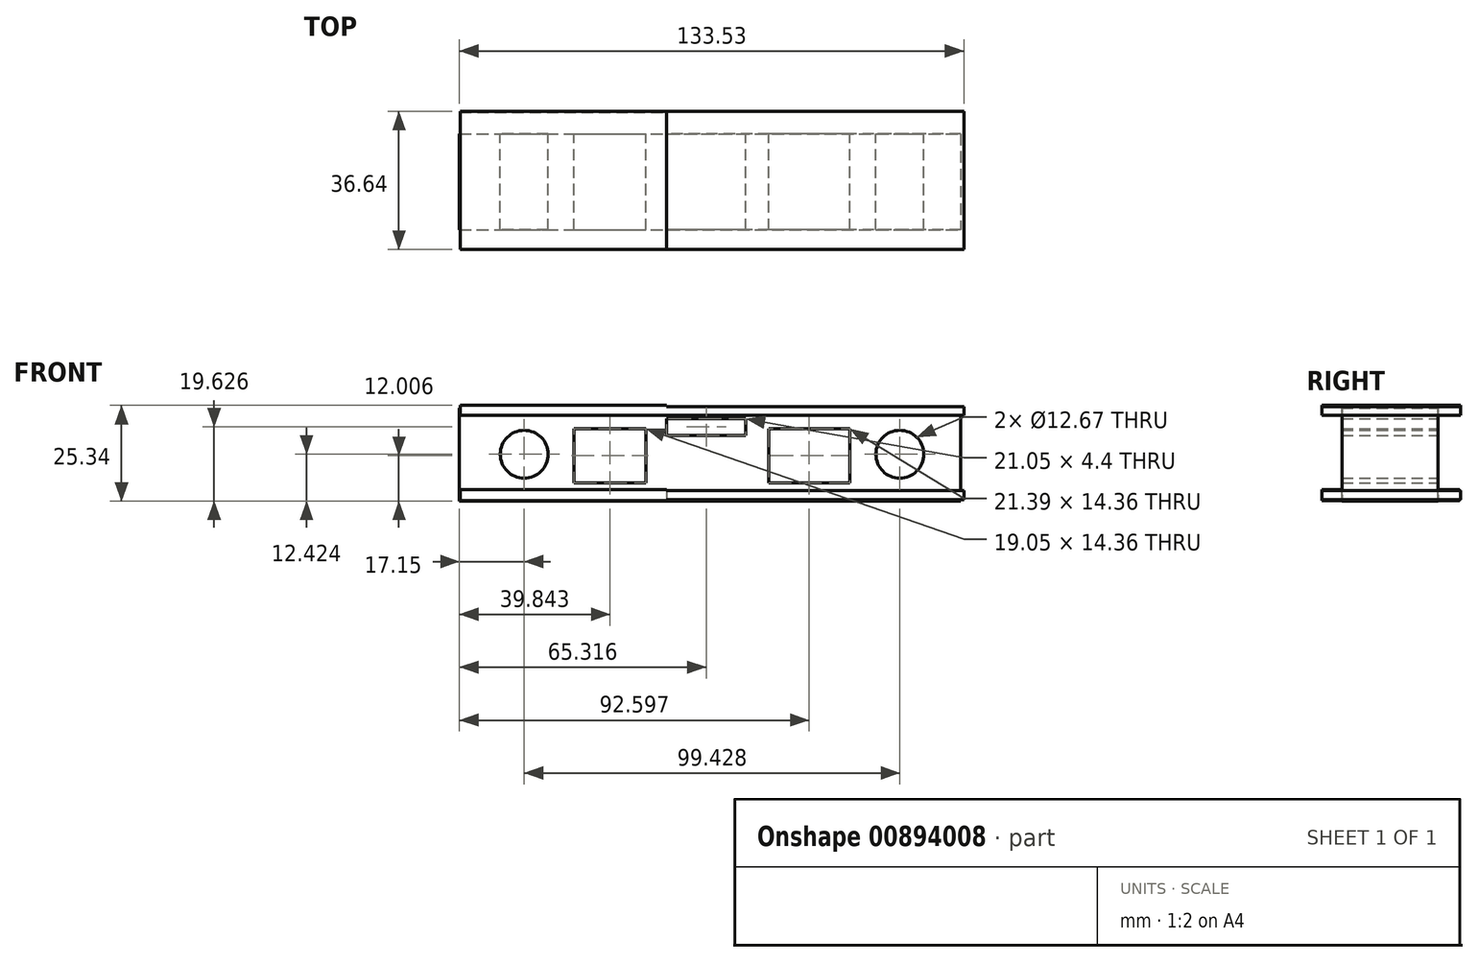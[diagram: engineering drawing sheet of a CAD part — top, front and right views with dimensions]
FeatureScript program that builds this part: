
annotation { "Feature Type Name" : "Feature", "Feature Type Description" : "" }
export const myFeature = defineFeature(function(context is Context, id is Id, definition is map)
    precondition{}
    {
        {
            var Q0;
            Q0=qCreatedBy(makeId("Front.planeOp"),FACE);
            var sketch = newSketch(context, id + "F0", { "sketchPlane" : qUnion([Q0])});
            skLineSegment(sketch, "E0.bottom", {"start": v(-54.8, 32.23) * mm, "end": v(77.94, 32.23) * mm});
            skLineSegment(sketch, "E0.top", {"start": v(-54.8, 7.63) * mm, "end": v(77.94, 7.63) * mm});
            skLineSegment(sketch, "E0.left", {"start": v(-54.8, 32.23) * mm, "end": v(-54.8, 7.63) * mm});
            skLineSegment(sketch, "E0.right", {"start": v(77.94, 32.23) * mm, "end": v(77.94, 7.63) * mm});
            skCircle(sketch, "E1", {"center": v(-37.64, 20.05) * mm, "radius": 6.34 * mm});
            skCircle(sketch, "E2", {"center": v(61.79, 20.05) * mm, "radius": 6.34 * mm});
            skLineSegment(sketch, "E3.bottom", {"start": v(-24.47, 26.82) * mm, "end": v(-5.42, 26.82) * mm});
            skLineSegment(sketch, "E3.top", {"start": v(-24.47, 12.46) * mm, "end": v(-5.42, 12.46) * mm});
            skLineSegment(sketch, "E3.left", {"start": v(-24.47, 26.82) * mm, "end": v(-24.47, 12.46) * mm});
            skLineSegment(sketch, "E3.right", {"start": v(-5.42, 26.82) * mm, "end": v(-5.42, 12.46) * mm});
            skLineSegment(sketch, "E4.bottom", {"start": v(48.5, 26.82) * mm, "end": v(27.1, 26.82) * mm});
            skLineSegment(sketch, "E4.top", {"start": v(48.5, 12.46) * mm, "end": v(27.1, 12.46) * mm});
            skLineSegment(sketch, "E4.left", {"start": v(48.5, 26.82) * mm, "end": v(48.5, 12.46) * mm});
            skLineSegment(sketch, "E4.right", {"start": v(27.1, 26.82) * mm, "end": v(27.1, 12.46) * mm});
            skSolve(sketch);
        }
        {
            var Q0;
            Q0 = qSketchRegion(id + "F0", true);
            extrude(context, id + "F1", {"entities" : qUnion([Q0]), "depth" : 25.4 * mm, "offsetDistance" : 25.4 * mm});
        }
        {
            var Q0;
            Q0=qCreatedBy(makeId("Right.planeOp"),FACE);
            var sketch = newSketch(context, id + "F2", { "sketchPlane" : qUnion([Q0])});
            skLineSegment(sketch, "E5.bottom", {"start": v(6, 32.68) * mm, "end": v(-30.63, 32.68) * mm});
            skLineSegment(sketch, "E5.top", {"start": v(6, 30.33) * mm, "end": v(-30.63, 30.33) * mm});
            skLineSegment(sketch, "E5.left", {"start": v(6, 32.68) * mm, "end": v(6, 30.33) * mm});
            skLineSegment(sketch, "E5.right", {"start": v(-30.63, 32.68) * mm, "end": v(-30.63, 30.33) * mm});
            skLineSegment(sketch, "E6.bottom", {"start": v(-30.63, 8.06) * mm, "end": v(6, 8.06) * mm});
            skLineSegment(sketch, "E6.top", {"start": v(-30.63, 10.4) * mm, "end": v(6, 10.4) * mm});
            skLineSegment(sketch, "E6.left", {"start": v(-30.63, 8.06) * mm, "end": v(-30.63, 10.4) * mm});
            skLineSegment(sketch, "E6.right", {"start": v(6, 8.06) * mm, "end": v(6, 10.4) * mm});
            skSolve(sketch);
        }
        {
            var Q0;
            Q0 = qSketchRegion(id + "F2", true);
            extrude(context, id + "F3", {"entities" : qUnion([Q0]), "operationType" : NewBodyOperationType.ADD, "depth" : 78.74 * mm, "offsetDistance" : 25.4 * mm});
        }
        {
            var Q0;
            Q0=qCreatedBy(makeId("Right.planeOp"),FACE);
            var sketch = newSketch(context, id + "F4", { "sketchPlane" : qUnion([Q0])});
            skLineSegment(sketch, "E7.bottom", {"start": v(-30.63, 32.97) * mm, "end": v(6, 32.97) * mm});
            skLineSegment(sketch, "E7.top", {"start": v(-30.63, 30.33) * mm, "end": v(6, 30.33) * mm});
            skLineSegment(sketch, "E7.left", {"start": v(-30.63, 32.97) * mm, "end": v(-30.63, 30.33) * mm});
            skLineSegment(sketch, "E7.right", {"start": v(6, 32.97) * mm, "end": v(6, 30.33) * mm});
            skLineSegment(sketch, "E8.bottom", {"start": v(-30.63, 10.7) * mm, "end": v(5.72, 10.7) * mm});
            skLineSegment(sketch, "E8.top", {"start": v(-30.63, 7.77) * mm, "end": v(5.72, 7.77) * mm});
            skLineSegment(sketch, "E8.left", {"start": v(-30.63, 10.7) * mm, "end": v(-30.63, 7.77) * mm});
            skLineSegment(sketch, "E8.right", {"start": v(5.72, 10.7) * mm, "end": v(5.72, 7.77) * mm});
            skSolve(sketch);
        }
        {
            var Q0;
            Q0 = qSketchRegion(id + "F4", true);
            extrude(context, id + "F5", {"entities" : qUnion([Q0]), "operationType" : NewBodyOperationType.ADD, "oppositeDirection" : true, "depth" : 54.6 * mm, "offsetDistance" : 25.4 * mm});
        }
        {
            var Q0;
            Q0=qCreatedBy(makeId("Front.planeOp"),FACE);
            var sketch = newSketch(context, id + "F6", { "sketchPlane" : qUnion([Q0])});
            skLineSegment(sketch, "E9.bottom", {"start": v(0, 29.45) * mm, "end": v(21.05, 29.45) * mm});
            skLineSegment(sketch, "E9.top", {"start": v(0, 25.06) * mm, "end": v(21.05, 25.06) * mm});
            skLineSegment(sketch, "E9.left", {"start": v(0, 29.45) * mm, "end": v(0, 25.06) * mm});
            skLineSegment(sketch, "E9.right", {"start": v(21.05, 29.45) * mm, "end": v(21.05, 25.06) * mm});
            skSolve(sketch);
        }
        {
            var Q0;
            Q0 = qSketchRegion(id + "F6", true);
            extrude(context, id + "F7", {"entities" : qUnion([Q0]), "operationType" : NewBodyOperationType.REMOVE, "depth" : 50.8 * mm, "offsetDistance" : 25.4 * mm});
        }
    });
